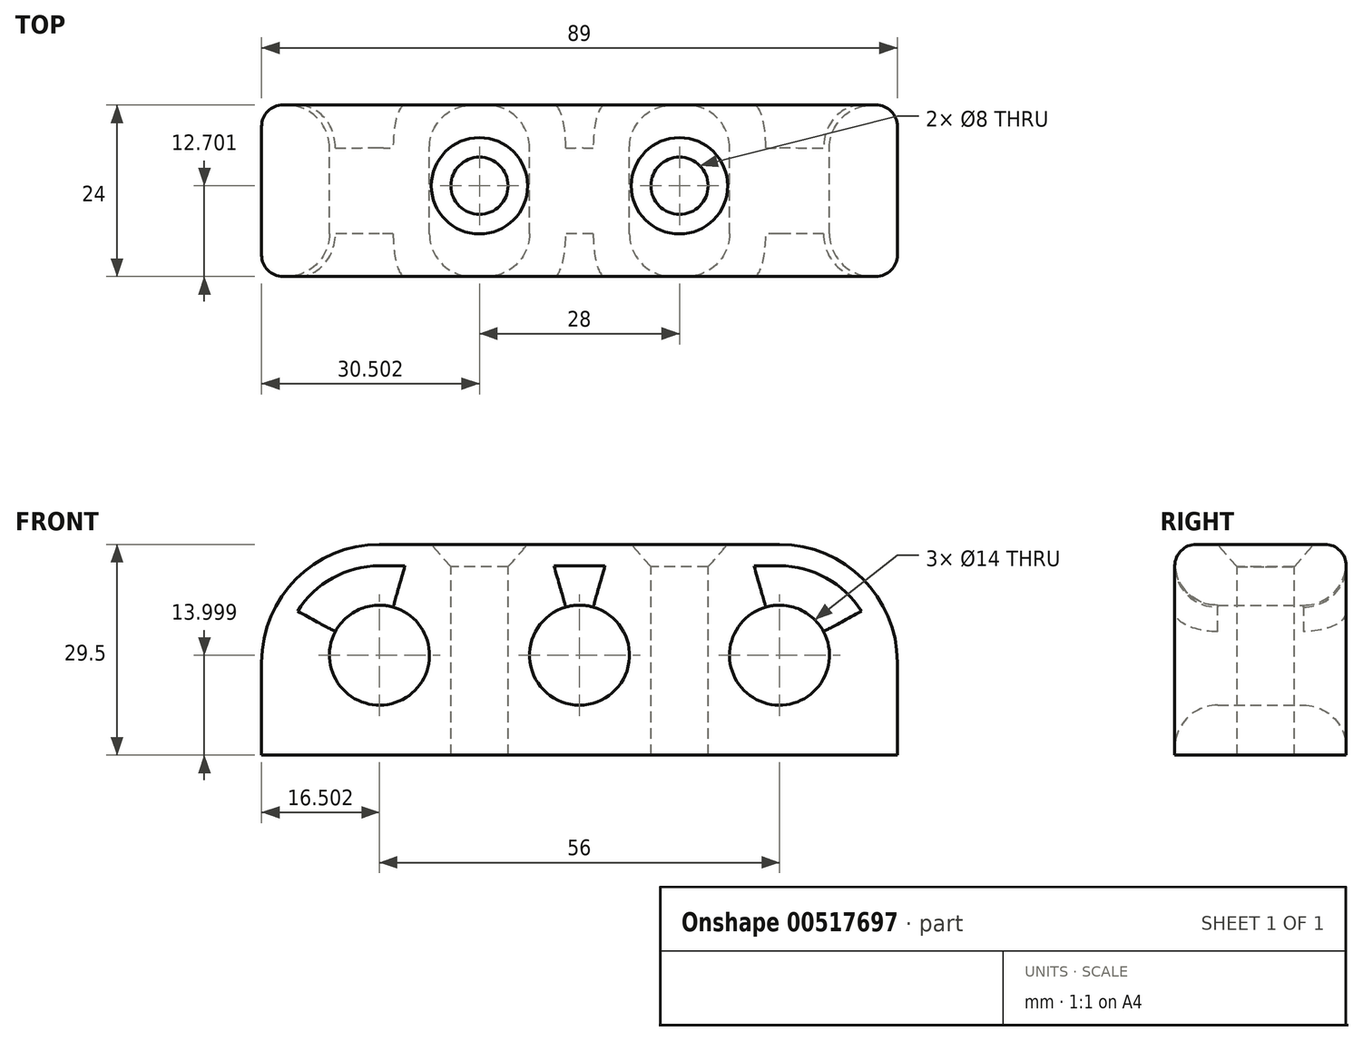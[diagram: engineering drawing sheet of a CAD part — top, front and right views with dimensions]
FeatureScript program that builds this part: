
annotation { "Feature Type Name" : "Feature", "Feature Type Description" : "" }
export const myFeature = defineFeature(function(context is Context, id is Id, definition is map)
    precondition{}
    {
        {
            var Q0;
            Q0=qCreatedBy(makeId("Front.planeOp"),FACE);
            var sketch = newSketch(context, id + "F0", { "sketchPlane" : qUnion([Q0])});
            skLineSegment(sketch, "E0", {"start": v(124.73, -82.62) * mm, "end": v(122.7, -82.62) * mm});
            skArc(sketch, "E1", {"start": v(122.7, -82.62) * mm, "mid": v(120.57, -83.5) * mm, "end": v(119.7, -85.62) * mm});
            skLineSegment(sketch, "E2", {"start": v(124.73, -106.62) * mm, "end": v(139.76, -106.62) * mm});
            skLineSegment(sketch, "E3", {"start": v(139.76, -82.62) * mm, "end": v(124.73, -82.62) * mm});
            skArc(sketch, "E4", {"start": v(119.7, -103.62) * mm, "mid": v(120.57, -105.74) * mm, "end": v(122.7, -106.62) * mm});
            skLineSegment(sketch, "E5", {"start": v(122.7, -106.62) * mm, "end": v(124.73, -106.62) * mm});
            skCircle(sketch, "E6", {"center": v(150.2, -94.62) * mm, "radius": 8.75 * mm});
            skLineSegment(sketch, "E7", {"start": v(119.7, -85.62) * mm, "end": v(119.7, -103.62) * mm});
            skLineSegment(sketch, "E8", {"start": v(188.62, -82.62) * mm, "end": v(167.76, -82.62) * mm});
            skFitSpline(sketch, "E9", {"points": [v(167.76, -82.62) * mm, v(166.78, -82.62) * mm, v(165.54, -82.65) * mm, v(164.2, -82.65) * mm]});
            skFitSpline(sketch, "E10", {"points": [v(160.62, -82.62) * mm, v(161.6, -82.62) * mm, v(162.85, -82.65) * mm, v(164.2, -82.65) * mm]});
            skLineSegment(sketch, "E11", {"start": v(139.76, -82.62) * mm, "end": v(160.62, -82.62) * mm});
            skArc(sketch, "E12", {"start": v(208.7, -85.62) * mm, "mid": v(207.81, -83.5) * mm, "end": v(205.7, -82.62) * mm});
            skLineSegment(sketch, "E13", {"start": v(203.66, -82.62) * mm, "end": v(205.7, -82.62) * mm});
            skFitSpline(sketch, "E14", {"points": [v(164.2, -106.58) * mm, v(163.54, -106.58) * mm, v(162.89, -106.6) * mm, v(161.66, -106.6) * mm, v(161.1, -106.62) * mm, v(160.62, -106.62) * mm]});
            skFitSpline(sketch, "E15", {"points": [v(164.2, -106.58) * mm, v(164.84, -106.58) * mm, v(165.5, -106.6) * mm, v(166.73, -106.6) * mm, v(167.27, -106.62) * mm, v(167.76, -106.62) * mm]});
            skArc(sketch, "E16", {"start": v(205.7, -106.62) * mm, "mid": v(207.81, -105.74) * mm, "end": v(208.7, -103.62) * mm});
            skLineSegment(sketch, "E17", {"start": v(205.7, -106.62) * mm, "end": v(203.66, -106.62) * mm});
            skLineSegment(sketch, "E18", {"start": v(167.76, -106.62) * mm, "end": v(188.62, -106.62) * mm});
            skLineSegment(sketch, "E19", {"start": v(160.62, -106.62) * mm, "end": v(139.76, -106.62) * mm});
            skLineSegment(sketch, "E20", {"start": v(160.62, -82.62) * mm, "end": v(167.76, -82.62) * mm});
            skLineSegment(sketch, "E21", {"start": v(160.62, -106.62) * mm, "end": v(167.76, -106.62) * mm});
            skLineSegment(sketch, "E22", {"start": v(203.66, -106.62) * mm, "end": v(188.62, -106.62) * mm});
            skLineSegment(sketch, "E23", {"start": v(188.62, -82.62) * mm, "end": v(203.66, -82.62) * mm});
            skCircle(sketch, "E24", {"center": v(178.2, -94.62) * mm, "radius": 8.75 * mm});
            skLineSegment(sketch, "E25", {"start": v(208.7, -85.62) * mm, "end": v(208.7, -103.62) * mm});
            skCircle(sketch, "E26", {"center": v(150.2, -94.62) * mm, "radius": 7.71 * mm});
            skCircle(sketch, "E27", {"center": v(150.2, -94.62) * mm, "radius": 4 * mm});
            skCircle(sketch, "E28", {"center": v(178.2, -94.62) * mm, "radius": 7.71 * mm});
            skCircle(sketch, "E29", {"center": v(178.2, -94.62) * mm, "radius": 4 * mm});
            skFitSpline(sketch, "E30", {"points": [v(136.2, -13.65) * mm, v(135.9, -13.65) * mm, v(135.61, -13.66) * mm, v(133.63, -13.79) * mm, v(131.97, -14.23) * mm, v(129.22, -15.58) * mm, v(128.1, -16.37) * mm, v(126.16, -18.24) * mm, v(125.35, -19.3) * mm, v(124.73, -20.48) * mm]});
            skArc(sketch, "E31", {"start": v(124.73, -20.48) * mm, "mid": v(141.27, -38.57) * mm, "end": v(139.76, -14.1) * mm});
            skFitSpline(sketch, "E32", {"points": [v(139.76, -14.1) * mm, v(139.7, -14.08) * mm, v(139.63, -14.06) * mm, v(138.6, -13.8) * mm, v(137.43, -13.65) * mm, v(136.2, -13.65) * mm]});
            skLineSegment(sketch, "E33", {"start": v(119.7, -40.6) * mm, "end": v(122.7, -40.6) * mm});
            skLineSegment(sketch, "E34", {"start": v(119.7, -40.6) * mm, "end": v(119.7, -27.6) * mm});
            skArc(sketch, "E35", {"start": v(122.18, -18.9) * mm, "mid": v(120.33, -23.07) * mm, "end": v(119.7, -27.6) * mm});
            skArc(sketch, "E36", {"start": v(136.2, -11.1) * mm, "mid": v(128.17, -13.18) * mm, "end": v(122.18, -18.9) * mm});
            skLineSegment(sketch, "E37", {"start": v(136.2, -11.1) * mm, "end": v(139.76, -11.1) * mm});
            skCircle(sketch, "E38", {"center": v(136.2, -26.6) * mm, "radius": 7 * mm});
            skFitSpline(sketch, "E39", {"points": [v(164.2, -13.65) * mm, v(163.54, -13.65) * mm, v(162.89, -13.69) * mm, v(161.66, -13.85) * mm, v(161.1, -13.96) * mm, v(160.62, -14.1) * mm]});
            skFitSpline(sketch, "E40", {"points": [v(164.2, -13.65) * mm, v(164.84, -13.65) * mm, v(165.5, -13.69) * mm, v(166.73, -13.85) * mm, v(167.27, -13.96) * mm, v(167.76, -14.1) * mm]});
            skFitSpline(sketch, "E41", {"points": [v(192.2, -13.65) * mm, v(192.48, -13.65) * mm, v(192.77, -13.66) * mm, v(194.76, -13.79) * mm, v(196.42, -14.23) * mm, v(199.17, -15.58) * mm, v(200.3, -16.37) * mm, v(202.23, -18.24) * mm, v(203.03, -19.3) * mm, v(203.66, -20.48) * mm]});
            skFitSpline(sketch, "E42", {"points": [v(188.62, -14.1) * mm, v(188.69, -14.08) * mm, v(188.75, -14.06) * mm, v(189.78, -13.8) * mm, v(190.95, -13.65) * mm, v(192.2, -13.65) * mm]});
            skLineSegment(sketch, "E43", {"start": v(208.7, -40.6) * mm, "end": v(205.7, -40.6) * mm});
            skLineSegment(sketch, "E44", {"start": v(208.7, -40.6) * mm, "end": v(208.7, -27.6) * mm});
            skArc(sketch, "E45", {"start": v(208.7, -27.6) * mm, "mid": v(208.06, -23.07) * mm, "end": v(206.2, -18.9) * mm});
            skArc(sketch, "E46", {"start": v(206.2, -18.9) * mm, "mid": v(200.2, -13.18) * mm, "end": v(192.2, -11.1) * mm});
            skLineSegment(sketch, "E47", {"start": v(139.76, -11.1) * mm, "end": v(188.62, -11.1) * mm});
            skLineSegment(sketch, "E48", {"start": v(192.2, -11.1) * mm, "end": v(188.62, -11.1) * mm});
            skArc(sketch, "E49", {"start": v(160.62, -14.1) * mm, "mid": v(164.2, -39.6) * mm, "end": v(167.76, -14.1) * mm});
            skCircle(sketch, "E50", {"center": v(164.2, -26.6) * mm, "radius": 7 * mm});
            skArc(sketch, "E51", {"start": v(188.62, -14.1) * mm, "mid": v(187.12, -38.57) * mm, "end": v(203.66, -20.48) * mm});
            skCircle(sketch, "E52", {"center": v(192.2, -26.6) * mm, "radius": 7 * mm});
            skLineSegment(sketch, "E53", {"start": v(205.7, -40.6) * mm, "end": v(122.7, -40.6) * mm});
            skFitSpline(sketch, "E54", {"points": [v(246.3, -13.65) * mm, v(246.3, -13.65) * mm, v(246.28, -13.7) * mm, v(246.27, -13.88) * mm, v(246.26, -13.98) * mm, v(246.26, -14.1) * mm, v(246.3, -13.65) * mm]});
            skArc(sketch, "E55", {"start": v(249.26, -11.1) * mm, "mid": v(247.3, -11.82) * mm, "end": v(246.3, -13.65) * mm});
            skLineSegment(sketch, "E56", {"start": v(246.26, -20.48) * mm, "end": v(246.26, -27.6) * mm});
            skLineSegment(sketch, "E57", {"start": v(246.26, -40.6) * mm, "end": v(249.26, -40.6) * mm});
            skLineSegment(sketch, "E58", {"start": v(246.26, -40.6) * mm, "end": v(246.26, -27.6) * mm});
            skFitSpline(sketch, "E59", {"points": [v(246.26, -20.48) * mm, v(246.26, -18.98) * mm, v(246.26, -17.67) * mm, v(246.28, -15.51) * mm, v(246.28, -14.7) * mm, v(246.3, -13.83) * mm, v(246.3, -13.65) * mm, v(246.3, -13.65) * mm, v(246.26, -20.48) * mm]});
            skFitSpline(sketch, "E60", {"points": [v(270.22, -13.65) * mm, v(270.22, -13.65) * mm, v(270.22, -13.66) * mm, v(270.23, -13.79) * mm, v(270.23, -14.23) * mm, v(270.24, -15.58) * mm, v(270.25, -16.37) * mm, v(270.25, -18.24) * mm, v(270.26, -19.3) * mm, v(270.26, -20.48) * mm, v(270.22, -13.65) * mm]});
            skLineSegment(sketch, "E61", {"start": v(270.26, -20.48) * mm, "end": v(270.26, -14.1) * mm});
            skFitSpline(sketch, "E62", {"points": [v(270.26, -14.1) * mm, v(270.26, -14.08) * mm, v(270.26, -14.06) * mm, v(270.25, -13.8) * mm, v(270.22, -13.65) * mm, v(270.22, -13.65) * mm, v(270.26, -14.1) * mm]});
            skLineSegment(sketch, "E63", {"start": v(246.26, -14.1) * mm, "end": v(246.26, -20.48) * mm});
            skLineSegment(sketch, "E64", {"start": v(267.26, -40.6) * mm, "end": v(270.26, -40.6) * mm});
            skLineSegment(sketch, "E65", {"start": v(270.26, -27.6) * mm, "end": v(270.26, -40.6) * mm});
            skLineSegment(sketch, "E66", {"start": v(270.26, -27.6) * mm, "end": v(270.26, -20.48) * mm});
            skArc(sketch, "E67", {"start": v(270.22, -13.65) * mm, "mid": v(269.21, -11.82) * mm, "end": v(267.26, -11.1) * mm});
            skLineSegment(sketch, "E68", {"start": v(249.26, -40.6) * mm, "end": v(267.26, -40.6) * mm});
            skLineSegment(sketch, "E69", {"start": v(249.26, -11.1) * mm, "end": v(267.26, -11.1) * mm});
            skLineSegment(sketch, "E70", {"start": v(138.7, -26.6) * mm, "end": v(133.7, -26.6) * mm});
            skLineSegment(sketch, "E71", {"start": v(136.2, -24.1) * mm, "end": v(136.2, -29.1) * mm});
            skLineSegment(sketch, "E72", {"start": v(166.7, -26.6) * mm, "end": v(161.7, -26.6) * mm});
            skLineSegment(sketch, "E73", {"start": v(164.2, -24.1) * mm, "end": v(164.2, -29.1) * mm});
            skLineSegment(sketch, "E74", {"start": v(194.7, -26.6) * mm, "end": v(189.7, -26.6) * mm});
            skLineSegment(sketch, "E75", {"start": v(192.2, -24.1) * mm, "end": v(192.2, -29.1) * mm});
            skLineSegment(sketch, "E76", {"start": v(184.7, -94.62) * mm, "end": v(171.7, -94.62) * mm});
            skLineSegment(sketch, "E77", {"start": v(178.2, -88.12) * mm, "end": v(178.2, -101.12) * mm});
            skLineSegment(sketch, "E78", {"start": v(156.7, -94.62) * mm, "end": v(143.7, -94.62) * mm});
            skLineSegment(sketch, "E79", {"start": v(150.2, -88.12) * mm, "end": v(150.2, -101.12) * mm});
            skSolve(sketch);
        }
        {
            var Q0;
            Q0=makeQuery(id+"F0.imprint","IMPRINT",FACE,{"disambiguationData":[TD([[makeQuery(id+"F0.imprint","IMPRINT",EDGE,{"derivedFrom":sQuery(id+"F0.wireOp",EDGE,"E30")}),1.0]])]});
            var Q1;
            Q1=makeQuery(id+"F0.imprint","IMPRINT",FACE,{"disambiguationData":[TD([[makeQuery(id+"F0.imprint","IMPRINT",EDGE,{"derivedFrom":sQuery(id+"F0.wireOp",EDGE,"E30")}),-1.0]])]});
            var Q2;
            Q2=makeQuery(id+"F0.imprint","IMPRINT",FACE,{"disambiguationData":[TD([[makeQuery(id+"F0.imprint","IMPRINT",EDGE,{"derivedFrom":sQuery(id+"F0.wireOp",EDGE,"E39")}),1.0]])]});
            var Q3;
            Q3=makeQuery(id+"F0.imprint","IMPRINT",FACE,{"disambiguationData":[TD([[makeQuery(id+"F0.imprint","IMPRINT",EDGE,{"derivedFrom":sQuery(id+"F0.wireOp",EDGE,"E41")}),-1.0]])]});
            extrude(context, id + "F1", {"entities" : qUnion([Q0, Q1, Q2, Q3]), "depth" : 24 * mm, "offsetDistance" : 25 * mm});
        }
        {
            var Q0;
            Q0=makeQuery(id+"F1.opExtrude","CAP_EDGE",EDGE,{"disambiguationData":[OSD([sQuery(id+"F0.wireOp",EDGE,"E34")])],"isStart":false});
            var Q1;
            Q1=makeQuery(id+"F1.opExtrude","CAP_EDGE",EDGE,{"disambiguationData":[OSD([sQuery(id+"F0.wireOp",EDGE,"E34")])],"isStart":true});
            fillet(context, id + "F2", {"entities" : qUnion([Q0, Q1]), "radius" : 3 * mm, "tangentPropagation" : true, "allowEdgeOverflow" : false});
        }
        {
            var Q0;
            Q0=makeQuery(id+"F1.opExtrude","SWEPT_FACE",FACE,{"disambiguationData":[OSD([sQuery(id+"F0.wireOp",EDGE,"E50")])]});
            var Q1;
            Q1=makeQuery(id+"F1.opExtrude","SWEPT_FACE",FACE,{"disambiguationData":[OSD([sQuery(id+"F0.wireOp",EDGE,"E38")])]});
            var Q2;
            Q2=makeQuery(id+"F1.opExtrude","SWEPT_FACE",FACE,{"disambiguationData":[OSD([sQuery(id+"F0.wireOp",EDGE,"E52")])]});
            fillet(context, id + "F3", {"entities" : qUnion([Q0, Q1, Q2]), "radius" : 6 * mm, "tangentPropagation" : true, "allowEdgeOverflow" : false});
        }
        {
            var Q0;
            Q0=makeQuery(id+"F1.opExtrude","SWEPT_FACE",FACE,{"disambiguationData":[OSD([sQuery(id+"F0.wireOp",EDGE,"E37"),sQuery(id+"F0.wireOp",EDGE,"E47"),sQuery(id+"F0.wireOp",EDGE,"E48")])]});
            var sketch = newSketch(context, id + "F4", { "sketchPlane" : qUnion([Q0])});
            skPoint(sketch, "E80", {"position": v(150.2, -11.3) * mm});
            skPoint(sketch, "E81", {"position": v(178.2, -11.3) * mm});
            skSolve(sketch);
        }
        {
            var Q0;
            Q0=sQuery(id+"F4.wireOp",VERTEX,"E80");
            var Q1;
            Q1=sQuery(id+"F4.wireOp",VERTEX,"E81");
            var Q2;
            Q2=makeQuery(id+"F1.opExtrude","SWEPT_BODY",BODY,{"disambiguationData":[OSD([sQuery(id+"F0.wireOp",EDGE,"E33"),sQuery(id+"F0.wireOp",EDGE,"E34"),sQuery(id+"F0.wireOp",EDGE,"E35"),sQuery(id+"F0.wireOp",EDGE,"E36"),sQuery(id+"F0.wireOp",EDGE,"E37"),sQuery(id+"F0.wireOp",EDGE,"E38"),sQuery(id+"F0.wireOp",EDGE,"E43"),sQuery(id+"F0.wireOp",EDGE,"E44"),sQuery(id+"F0.wireOp",EDGE,"E45"),sQuery(id+"F0.wireOp",EDGE,"E46"),sQuery(id+"F0.wireOp",EDGE,"E47"),sQuery(id+"F0.wireOp",EDGE,"E48"),sQuery(id+"F0.wireOp",EDGE,"E50"),sQuery(id+"F0.wireOp",EDGE,"E52"),sQuery(id+"F0.wireOp",EDGE,"E53")])]});
            hole(context, id + "F5", {"style" : HoleStyle.C_SINK, "endStyle" : HoleEndStyle.THROUGH, "holeDiameter" : 8 * mm, "cSinkDiameter" : 13.5 * mm, "cSinkAngle" : 82 * degree, "isTappedThrough" : true, "tappedDepth" : 12 * mm, "tapClearance" : 3, "locations" : qUnion([Q0, Q1]), "scope" : qUnion([Q2])});
        }
    });
